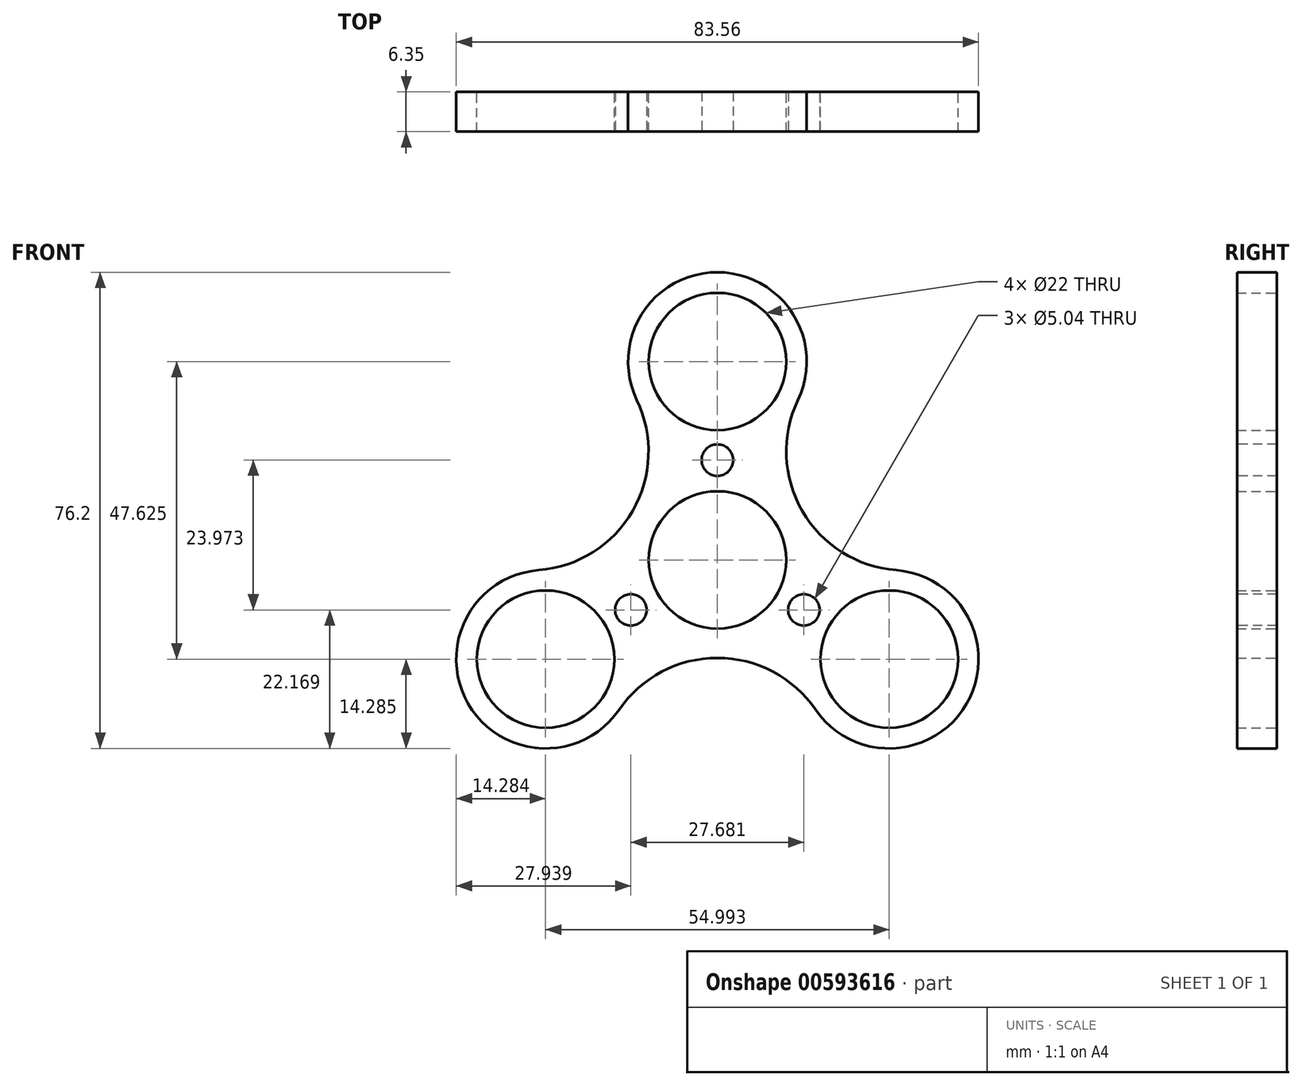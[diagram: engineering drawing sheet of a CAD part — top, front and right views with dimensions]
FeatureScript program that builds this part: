
annotation { "Feature Type Name" : "Feature", "Feature Type Description" : "" }
export const myFeature = defineFeature(function(context is Context, id is Id, definition is map)
    precondition{}
    {
        {
            var Q0;
            Q0=qCreatedBy(makeId("Front.planeOp"),FACE);
            var sketch = newSketch(context, id + "F0", { "sketchPlane" : qUnion([Q0])});
            skCircle(sketch, "E0", {"center": v(0, 0) * mm, "radius": 14.29 * mm});
            skCircle(sketch, "E1", {"center": v(0, 0) * mm, "radius": 11 * mm});
            skCircle(sketch, "E2", {"center": v(0, 31.75) * mm, "radius": 14.29 * mm});
            skCircle(sketch, "E3", {"center": v(0, 31.75) * mm, "radius": 11 * mm});
            skCircle(sketch, "E4.1.0", {"center": v(-27.5, -15.87) * mm, "radius": 14.29 * mm});
            skCircle(sketch, "E4.1.1", {"center": v(-27.5, -15.87) * mm, "radius": 11 * mm});
            skCircle(sketch, "E4.2.0", {"center": v(27.5, -15.88) * mm, "radius": 14.29 * mm});
            skCircle(sketch, "E4.2.1", {"center": v(27.5, -15.88) * mm, "radius": 11 * mm});
            skSolve(sketch);
        }
        {
            var Q0;
            Q0=qCreatedBy(makeId("Front.planeOp"),FACE);
            var sketch = newSketch(context, id + "F1", { "sketchPlane" : qUnion([Q0])});
            skCircle(sketch, "E5", {"center": v(-30.07, 17.36) * mm, "radius": 19.05 * mm});
            skCircle(sketch, "E6", {"center": v(30.07, 17.36) * mm, "radius": 19.05 * mm});
            skCircle(sketch, "E7", {"center": v(0, -34.73) * mm, "radius": 19.05 * mm});
            skCircle(sketch, "E8.1", {"center": v(0, 31.75) * mm, "radius": 14.29 * mm});
            skCircle(sketch, "E8.2", {"center": v(0, 31.75) * mm, "radius": 11 * mm});
            skCircle(sketch, "E8.3", {"center": v(0, 0) * mm, "radius": 14.29 * mm});
            skCircle(sketch, "E8.4", {"center": v(0, 0) * mm, "radius": 11 * mm});
            skCircle(sketch, "E8.6", {"center": v(27.5, -15.88) * mm, "radius": 14.29 * mm});
            skCircle(sketch, "E8.7", {"center": v(27.5, -15.88) * mm, "radius": 11 * mm});
            skCircle(sketch, "E8.9", {"center": v(-27.5, -15.87) * mm, "radius": 14.29 * mm});
            skCircle(sketch, "E8.10", {"center": v(-27.5, -15.87) * mm, "radius": 11 * mm});
            skSolve(sketch);
        }
        {
            var Q0;
            Q0=makeQuery(id+"F1.imprint","IMPRINT",FACE,{"disambiguationData":[TD([[makeQuery(id+"F1.imprint","IMPRINT",EDGE,{"derivedFrom":sQuery(id+"F1.wireOp",EDGE,"E8.2")}),-1.0]])]});
            var Q1;
            Q1=makeQuery(id+"F1.imprint","IMPRINT",FACE,{"disambiguationData":[TD([[makeQuery(id+"F1.imprint","IMPRINT",EDGE,{"derivedFrom":sQuery(id+"F1.wireOp",EDGE,"E8.7")}),-1.0]])]});
            var Q2;
            Q2=makeQuery(id+"F1.imprint","IMPRINT",FACE,{"disambiguationData":[TD([[makeQuery(id+"F1.imprint","IMPRINT",EDGE,{"derivedFrom":sQuery(id+"F1.wireOp",EDGE,"E8.10")}),-1.0]])]});
            var Q3;
            Q3=makeQuery(id+"F1.imprint","IMPRINT",FACE,{"disambiguationData":[TD([[makeQuery(id+"F1.imprint","IMPRINT",EDGE,{"derivedFrom":sQuery(id+"F1.wireOp",EDGE,"E8.3")}),-1.0]])]});
            extrude(context, id + "F2", {"entities" : qUnion([Q0, Q1, Q2, Q3]), "depth" : 6.35 * mm, "offsetDistance" : 25.4 * mm});
        }
        {
            var Q0;
            Q0=makeQuery(id+"F0.imprint","IMPRINT",FACE,{"disambiguationData":[TD([[makeQuery(id+"F0.imprint","IMPRINT",EDGE,{"derivedFrom":sQuery(id+"F0.wireOp",EDGE,"E0")}),1.0]])]});
            extrude(context, id + "F3", {"entities" : qUnion([Q0]), "operationType" : NewBodyOperationType.ADD, "depth" : 6.35 * mm, "offsetDistance" : 25.4 * mm});
        }
        {
            var Q0;
            Q0=makeQuery(id+"F3.boolean.opBoolean","MERGE",FACE,{"derivedFrom":[makeQuery(id+"F2.opExtrude","CAP_FACE",FACE,{"disambiguationData":[OSD([sQuery(id+"F1.wireOp",EDGE,"E5"),sQuery(id+"F1.wireOp",EDGE,"E6"),sQuery(id+"F1.wireOp",EDGE,"E7"),sQuery(id+"F1.wireOp",EDGE,"E8.1"),sQuery(id+"F1.wireOp",EDGE,"E8.2"),sQuery(id+"F1.wireOp",EDGE,"E8.3"),sQuery(id+"F1.wireOp",EDGE,"E8.6"),sQuery(id+"F1.wireOp",EDGE,"E8.7"),sQuery(id+"F1.wireOp",EDGE,"E8.9"),sQuery(id+"F1.wireOp",EDGE,"E8.10")])],"isStart":false}),makeQuery(id+"F3.opExtrude","CAP_FACE",FACE,{"disambiguationData":[OSD([sQuery(id+"F0.wireOp",EDGE,"E0"),sQuery(id+"F0.wireOp",EDGE,"E1")])],"isStart":false})]});
            var sketch = newSketch(context, id + "F4", { "sketchPlane" : qUnion([Q0])});
            skCircle(sketch, "E9", {"center": v(0, 15.98) * mm, "radius": 2.52 * mm});
            skCircle(sketch, "E10.1.0", {"center": v(-13.84, -8) * mm, "radius": 2.52 * mm});
            skCircle(sketch, "E10.2.0", {"center": v(13.84, -8) * mm, "radius": 2.52 * mm});
            skPoint(sketch, "E10.center", {"position": v(0, 0) * mm});
            skSolve(sketch);
        }
        {
            var Q0;
            Q0=makeQuery(id+"F4.imprint","IMPRINT",FACE,{"disambiguationData":[TD([[makeQuery(id+"F4.imprint","IMPRINT",EDGE,{"derivedFrom":sQuery(id+"F4.wireOp",EDGE,"E9")}),1.0]])]});
            var Q1;
            Q1=makeQuery(id+"F4.imprint","IMPRINT",FACE,{"disambiguationData":[TD([[makeQuery(id+"F4.imprint","IMPRINT",EDGE,{"derivedFrom":sQuery(id+"F4.wireOp",EDGE,"E10.1.0")}),1.0]])]});
            var Q2;
            Q2=makeQuery(id+"F4.imprint","IMPRINT",FACE,{"disambiguationData":[TD([[makeQuery(id+"F4.imprint","IMPRINT",EDGE,{"derivedFrom":sQuery(id+"F4.wireOp",EDGE,"E10.2.0")}),1.0]])]});
            var Q3;
            Q3=sQuery(id+"F4.wireOp",EDGE,"E9");
            var Q4;
            Q4=sQuery(id+"F4.wireOp",EDGE,"E10.1.0");
            var Q5;
            Q5=sQuery(id+"F4.wireOp",EDGE,"E10.2.0");
            extrude(context, id + "F5", {"entities" : qUnion([Q0, Q1, Q2]), "operationType" : NewBodyOperationType.REMOVE, "surfaceEntities" : qUnion([Q3, Q4, Q5]), "endBound" : BoundingType.THROUGH_ALL, "oppositeDirection" : true, "depth" : 25.4 * mm, "offsetDistance" : 25.4 * mm});
        }
    });
